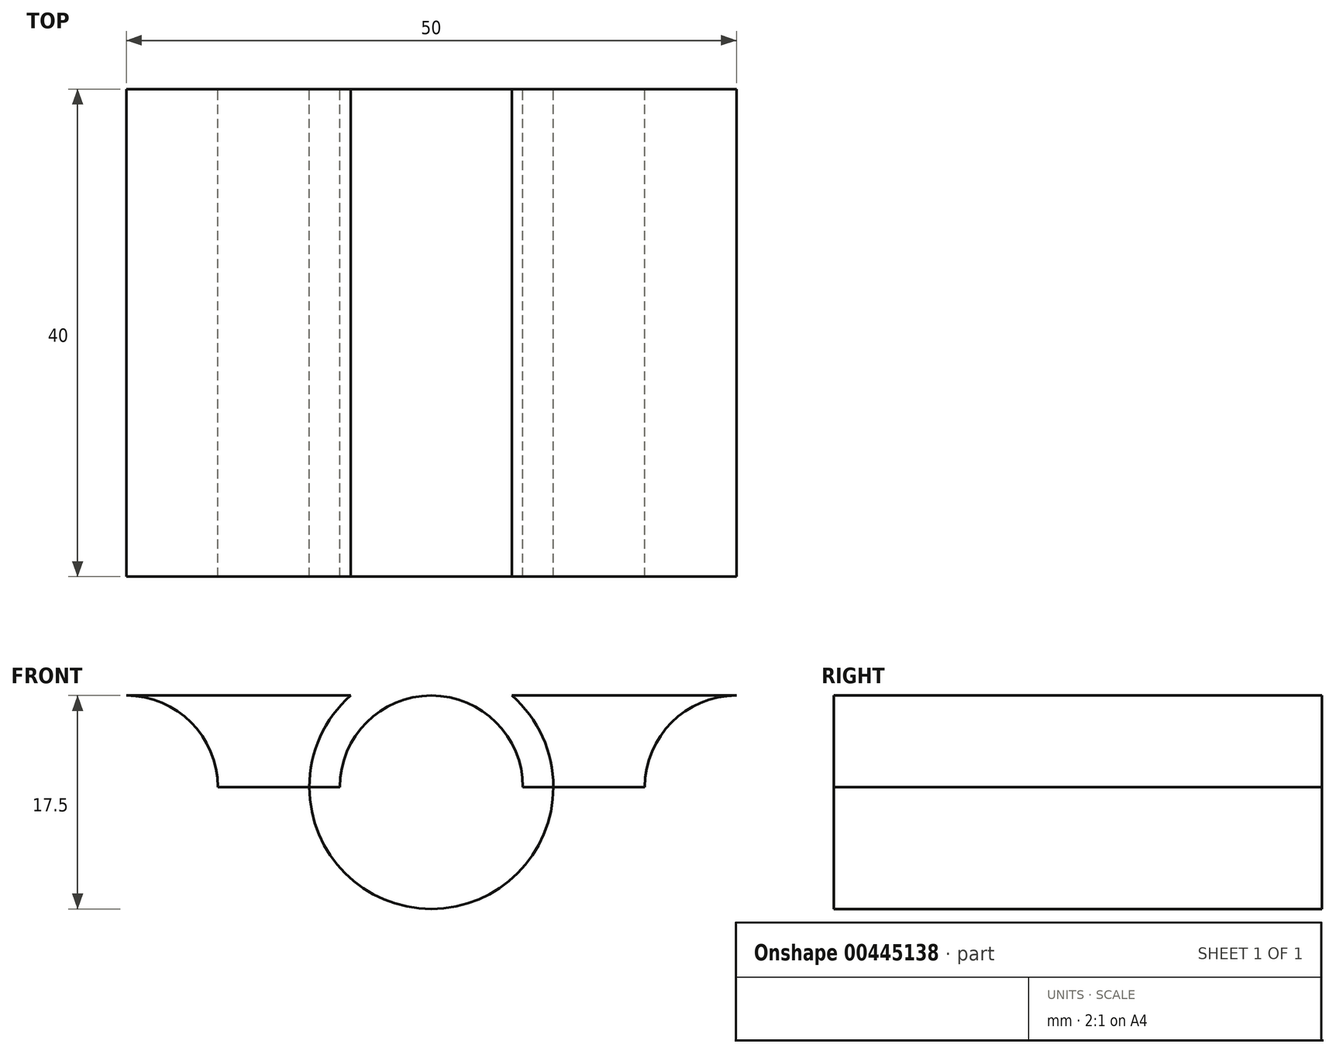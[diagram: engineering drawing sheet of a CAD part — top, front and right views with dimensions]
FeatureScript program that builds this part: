
annotation { "Feature Type Name" : "Feature", "Feature Type Description" : "" }
export const myFeature = defineFeature(function(context is Context, id is Id, definition is map)
    precondition{}
    {
        {
            var Q0;
            Q0=qCreatedBy(makeId("Front.planeOp"),FACE);
            var sketch = newSketch(context, id + "F0", { "sketchPlane" : qUnion([Q0])});
            skLineSegment(sketch, "E0.bottom", {"start": v(32.5, 7.5) * mm, "end": v(-32.5, 7.5) * mm});
            skLineSegment(sketch, "E0.top", {"start": v(32.5, -7.5) * mm, "end": v(-32.5, -7.5) * mm});
            skLineSegment(sketch, "E0.left", {"start": v(32.5, 7.5) * mm, "end": v(32.5, -7.5) * mm});
            skLineSegment(sketch, "E0.right", {"start": v(-32.5, 7.5) * mm, "end": v(-32.5, -7.5) * mm});
            skPoint(sketch, "E0.middle", {"position": v(0, 0) * mm});
            skCircle(sketch, "E1", {"center": v(25, 0) * mm, "radius": 7.5 * mm});
            skCircle(sketch, "E2", {"center": v(-25, 0) * mm, "radius": 7.5 * mm});
            skCircle(sketch, "E3", {"center": v(0, 0) * mm, "radius": 7.5 * mm});
            skLineSegment(sketch, "E4", {"start": v(-17.5, 0) * mm, "end": v(-7.5, 0) * mm});
            skLineSegment(sketch, "E5", {"start": v(17.5, 0) * mm, "end": v(7.5, 0) * mm});
            skCircle(sketch, "E6", {"center": v(0, 0) * mm, "radius": 10 * mm});
            skSolve(sketch);
        }
        {
            var Q0;
            {var subQ0=sQuery(id+"F0.wireOp",EDGE,"E6");var subQ1=sQuery(id+"F0.wireOp",EDGE,"E0.top");var subQ2=makeQuery(id+"F0.imprint","INTERSECT",VERTEX,{"disambiguationData":[OD(0.0)],"derivedFrom":[subQ1,subQ0]});Q0=makeQuery(id+"F0.imprint","IMPRINT",FACE,{"disambiguationData":[TD([[makeQuery(id+"F0.imprint","IMPRINT",EDGE,{"disambiguationData":[TD([[subQ2,-1.0]])],"derivedFrom":subQ1}),1.0]])]});}
            var Q1;
            {var subQ0=sQuery(id+"F0.wireOp",EDGE,"E6");var subQ1=sQuery(id+"F0.wireOp",EDGE,"E0.top");var subQ2=makeQuery(id+"F0.imprint","INTERSECT",VERTEX,{"disambiguationData":[OD(0.0)],"derivedFrom":[subQ1,subQ0]});Q1=makeQuery(id+"F0.imprint","IMPRINT",FACE,{"disambiguationData":[TD([[makeQuery(id+"F0.imprint","IMPRINT",EDGE,{"disambiguationData":[TD([[subQ2,-1.0]])],"derivedFrom":subQ1}),-1.0]])]});}
            var Q2;
            {var subQ0=sQuery(id+"F0.wireOp",EDGE,"E6");var subQ1=sQuery(id+"F0.wireOp",EDGE,"E0.bottom");var subQ2=makeQuery(id+"F0.imprint","INTERSECT",VERTEX,{"disambiguationData":[OD(0.0)],"derivedFrom":[subQ1,subQ0]});Q2=makeQuery(id+"F0.imprint","IMPRINT",FACE,{"disambiguationData":[TD([[makeQuery(id+"F0.imprint","IMPRINT",EDGE,{"disambiguationData":[TD([[subQ2,-1.0]])],"derivedFrom":subQ1}),1.0]])]});}
            var Q3;
            {var subQ0=sQuery(id+"F0.wireOp",EDGE,"E6");var subQ1=sQuery(id+"F0.wireOp",EDGE,"E0.bottom");var subQ2=makeQuery(id+"F0.imprint","INTERSECT",VERTEX,{"disambiguationData":[OD(0.0)],"derivedFrom":[subQ1,subQ0]});Q3=makeQuery(id+"F0.imprint","IMPRINT",FACE,{"disambiguationData":[TD([[makeQuery(id+"F0.imprint","IMPRINT",EDGE,{"disambiguationData":[TD([[subQ2,-1.0]])],"derivedFrom":subQ1}),-1.0]])]});}
            var Q4;
            {var subQ0=sQuery(id+"F0.wireOp",EDGE,"E6");var subQ1=sQuery(id+"F0.wireOp",EDGE,"E0.bottom");var subQ2=makeQuery(id+"F0.imprint","INTERSECT",VERTEX,{"disambiguationData":[OD(1.0)],"derivedFrom":[subQ1,subQ0]});Q4=makeQuery(id+"F0.imprint","IMPRINT",FACE,{"disambiguationData":[TD([[makeQuery(id+"F0.imprint","IMPRINT",EDGE,{"disambiguationData":[TD([[subQ2,1.0]])],"derivedFrom":subQ1}),1.0]])]});}
            var Q5;
            {var subQ0=sQuery(id+"F0.wireOp",EDGE,"E6");var subQ1=sQuery(id+"F0.wireOp",EDGE,"E0.top");var subQ2=makeQuery(id+"F0.imprint","INTERSECT",VERTEX,{"disambiguationData":[OD(1.0)],"derivedFrom":[subQ1,subQ0]});Q5=makeQuery(id+"F0.imprint","IMPRINT",FACE,{"disambiguationData":[TD([[makeQuery(id+"F0.imprint","IMPRINT",EDGE,{"disambiguationData":[TD([[subQ2,1.0]])],"derivedFrom":subQ1}),-1.0]])]});}
            var Q6;
            {var subQ0=sQuery(id+"F0.wireOp",EDGE,"E3");var subQ1=makeQuery(id+"F0.imprint","INTERSECT",VERTEX,{"derivedFrom":[subQ0,sQuery(id+"F0.wireOp",EDGE,"E5")]});Q6=makeQuery(id+"F0.imprint","IMPRINT",FACE,{"disambiguationData":[TD([[makeQuery(id+"F0.imprint","IMPRINT",EDGE,{"disambiguationData":[TD([[subQ1,-1.0]])],"derivedFrom":subQ0}),1.0]])]});}
            extrude(context, id + "F1", {"entities" : qUnion([Q0, Q1, Q2, Q3, Q4, Q5, Q6]), "depth" : 40 * mm});
        }
    });
